# Revit family: Ghent - Recessed Wall Case - 900DC2
name_source: partatom
category: Furniture
units: mm (PartAtom-declared; Revit-internal decimal feet)

## family parameters
Always vertical = Yes
Cut with Voids When Loaded = No
Host = Wall
Room Calculation Point = No
Shared = No

## types (3) — shared parameters
2D Door Swing Angle = 45.00°
Case Protrusion = 0' - 0"
Description = Waddell Display Case - Recessed Series
Manufacturer = Ghent
Max Opening Width = 22' - 0"
Show 2D Plan Graphics = Yes
URL = https://ghent.com

## per-type parameters (varying)
| type | Door Type Control | Max Opening Height | Model | Overlap |
| 1/4" Tempered Glass Minimally Framed Sliding Doors | 2 | 6' - 2" | 900DC-MF | 0' - 1 1/16" |
| 3/16" Tempered Glass Fully Framed Sliding Doors | 1 | 7' - 4" | 900DC-FF | 0' - 1 1/8" |
| 3/8" Tempered Glass Pivoting Doors | 0 | 8' - 1" | 900DC-PVT | 0' - 0" |

## geometry (parser evidence)
native form markers: Sweep x18
no freeform markers — native parametric forms only
